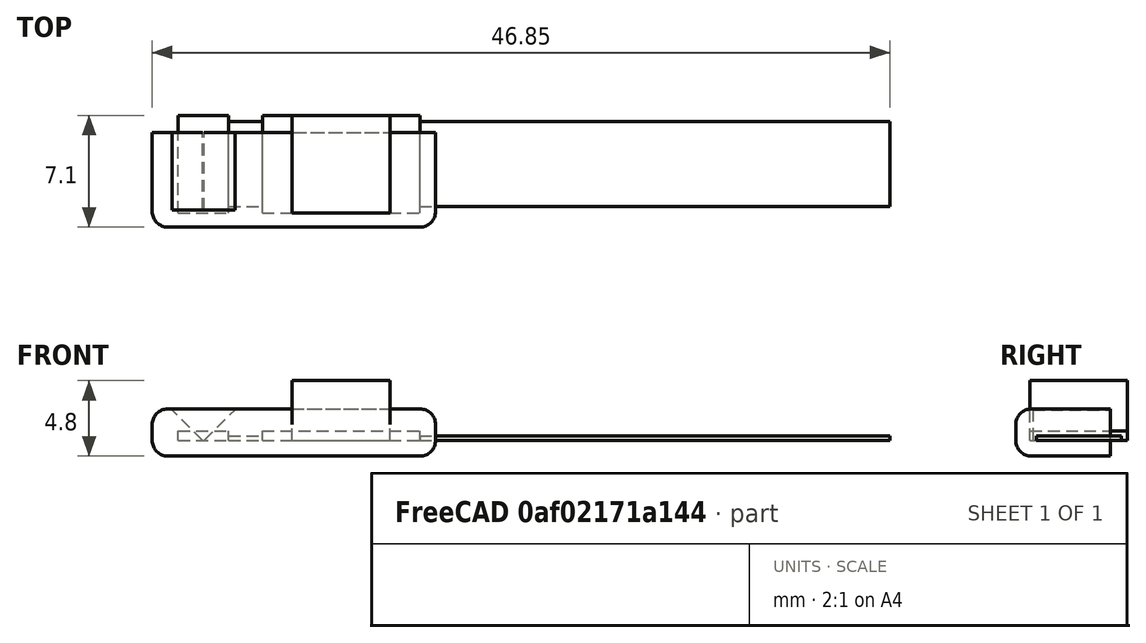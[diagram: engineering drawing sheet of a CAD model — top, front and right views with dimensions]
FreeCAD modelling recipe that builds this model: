
FCSTD DOCUMENT  (FreeCAD 0.17R13519 (Git))
Label: METHVEx_CameraHolder
License: All rights reserved
LicenseURL: http://en.wikipedia.org/wiki/All_rights_reserved
objects: Part::Box×8, Part::MultiFuse×1, Part::Fillet×1, Part::Chamfer×1, Part::Cut×1
note: 12 computed .brp shape members not serialized (recipe doc carries the construction recipe); baked Part::Feature solids carry a one-line shape summary decoded from their .brp

FEATURE [Part::Box] Box  label="Camera"
  AttacherType = Attacher::AttachEngine3D
  Height = 3.8
  Length = 6.2
  Placement = pos=(-3.1,-3.1,0) rot=(0,0,1;0rad)
  Width = 6.2
FEATURE [Part::Box] Box001  label="Cube"
  AttacherType = Attacher::AttachEngine3D
  Height = 0.6
  Length = 10
  Placement = pos=(-5,-3.1,0) rot=(0,0,1;0rad)
  Width = 6.2
FEATURE [Part::Box] Box002  label="Cube001"
  AttacherType = Attacher::AttachEngine3D
  Height = 0.3
  Length = 2.15
  Placement = pos=(-7.15,-2.7,0) rot=(0,0,1;0rad)
  Width = 5.4
FEATURE [Part::Box] Box003  label="Cube002"
  AttacherType = Attacher::AttachEngine3D
  Height = 0.6
  Length = 3.2
  Placement = pos=(-10.35,-3.1,0) rot=(0,0,1;0rad)
  Width = 6.2
FEATURE [Part::Box] Box004  label="Cube003"
  AttacherType = Attacher::AttachEngine3D
  Height = 0.3
  Length = 30
  Placement = pos=(4.85,-2.7,0) rot=(0,0,1;0rad)
  Width = 5.4
FEATURE [Part::Box] Box005  label="Cube004"
  AttacherType = Attacher::AttachEngine3D
  Height = 3
  Length = 18
  Placement = pos=(-12,-4,-1) rot=(0,0,1;0rad)
  Width = 6
FEATURE [Part::MultiFuse] Fusion
  Shapes = -> [Box004,Box003,Box002,Box001]
FEATURE [Part::Box] Box006  label="Camera001"
  AttacherType = Attacher::AttachEngine3D
  Height = 3.8
  Length = 6.2
  Placement = pos=(-3.1,-3.1,0) rot=(0,0,1;0rad)
  Width = 6.2
FEATURE [Part::Fillet] Fillet
  Base = -> Box005
  Edges = 8 edges r=1: [Edge1,Edge2,Edge4,Edge5,Edge6,Edge8,Edge9,Edge10]
FEATURE [Part::Box] Box007  label="Cube005"
  AttacherType = Attacher::AttachEngine3D
  Height = 3
  Length = 4
  Placement = pos=(-10.75,-3.1,0) rot=(0,0,1;0rad)
  Width = 6.2
FEATURE [Part::Chamfer] Chamfer
  Base = -> Box007
  Edges = 2 edges r=1.95: [Edge4,Edge8]
  Placement = pos=(0,0.2,0) rot=(0,0,1;0rad)
FEATURE [Part::Cut] Cut
  Base = -> Fillet
  Tool = -> Chamfer
